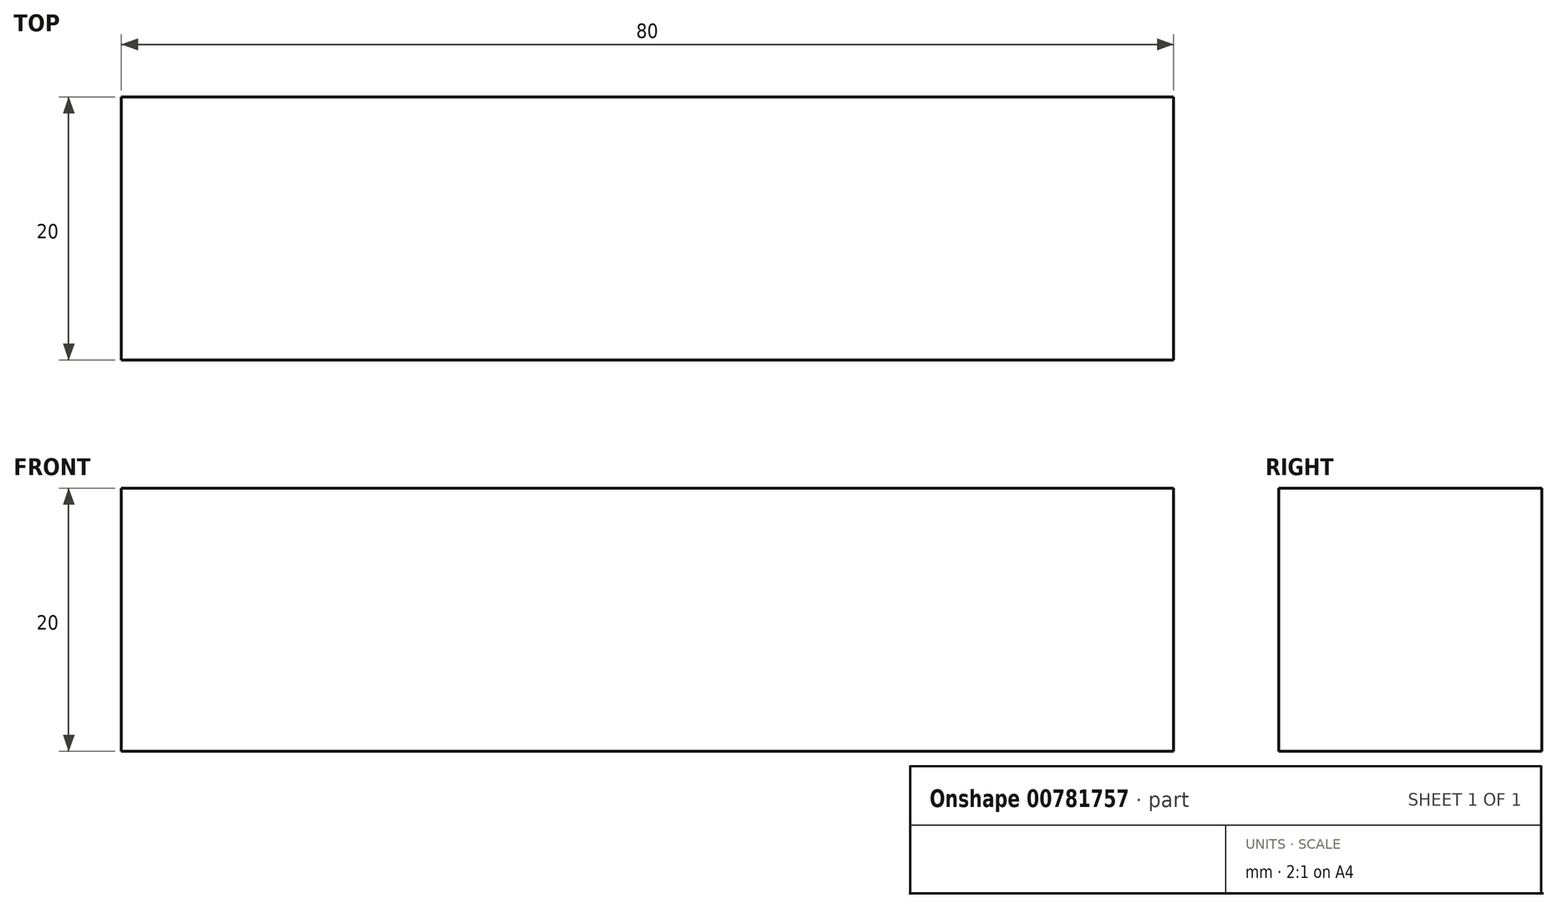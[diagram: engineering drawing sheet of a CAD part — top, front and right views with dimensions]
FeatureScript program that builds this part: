
annotation { "Feature Type Name" : "Feature", "Feature Type Description" : "" }
export const myFeature = defineFeature(function(context is Context, id is Id, definition is map)
    precondition{}
    {
        {
            var Q0;
            Q0=qCreatedBy(makeId("Top.planeOp"),FACE);
            var sketch = newSketch(context, id + "F0", { "sketchPlane" : qUnion([Q0])});
            skLineSegment(sketch, "E0.bottom", {"start": v(-28.64, 7.97) * mm, "end": v(51.36, 7.97) * mm});
            skLineSegment(sketch, "E0.top", {"start": v(-28.64, -12.03) * mm, "end": v(51.36, -12.03) * mm});
            skLineSegment(sketch, "E0.left", {"start": v(-28.64, 7.97) * mm, "end": v(-28.64, -12.03) * mm});
            skLineSegment(sketch, "E0.right", {"start": v(51.36, 7.97) * mm, "end": v(51.36, -12.03) * mm});
            skSolve(sketch);
        }
        {
            var Q0;
            Q0=makeQuery(id+"F0.imprint","IMPRINT",FACE,{"disambiguationData":[TD([[makeQuery(id+"F0.imprint","IMPRINT",EDGE,{"derivedFrom":sQuery(id+"F0.wireOp",EDGE,"E0.top")}),1.0]])]});
            extrude(context, id + "F1", {"entities" : qUnion([Q0]), "depth" : 20 * mm, "offsetDistance" : 25 * mm});
        }
    });
